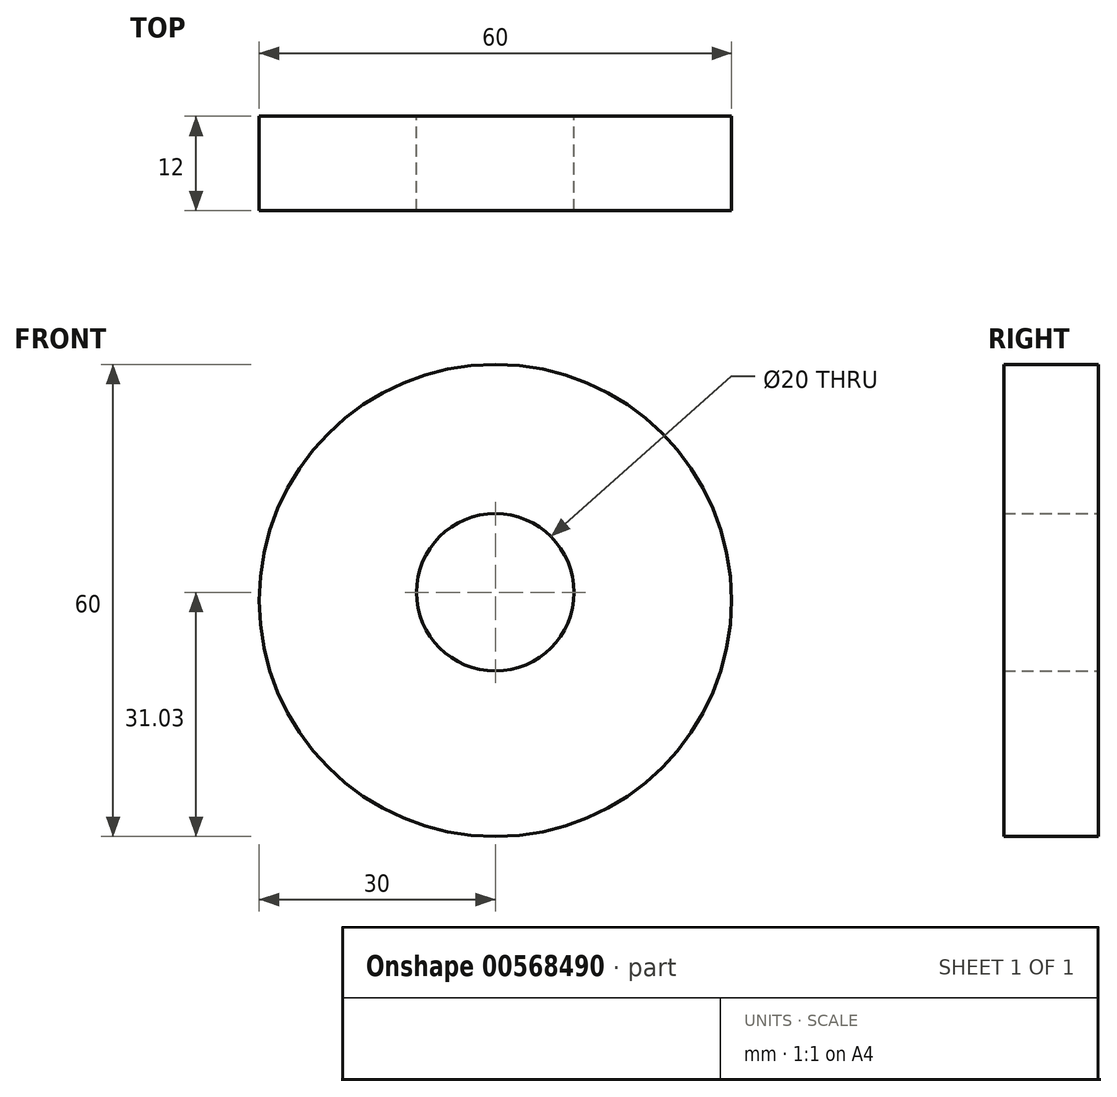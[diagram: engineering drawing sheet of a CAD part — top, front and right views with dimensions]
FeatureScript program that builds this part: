
annotation { "Feature Type Name" : "Feature", "Feature Type Description" : "" }
export const myFeature = defineFeature(function(context is Context, id is Id, definition is map)
    precondition{}
    {
        {
            var Q0;
            Q0=qCreatedBy(makeId("Front.planeOp"),FACE);
            var sketch = newSketch(context, id + "F0", { "sketchPlane" : qUnion([Q0])});
            skCircle(sketch, "E0", {"center": v(0, -1.03) * mm, "radius": 30 * mm});
            skCircle(sketch, "E1", {"center": v(0, 0) * mm, "radius": 10 * mm});
            skSolve(sketch);
        }
        {
            var Q0;
            Q0=makeQuery(id+"F0.imprint","IMPRINT",FACE,{"disambiguationData":[TD([[makeQuery(id+"F0.imprint","IMPRINT",EDGE,{"derivedFrom":sQuery(id+"F0.wireOp",EDGE,"E0")}),1.0]])]});
            extrude(context, id + "F1", {"entities" : qUnion([Q0]), "endBound" : BoundingType.SYMMETRIC, "depth" : 12 * mm, "offsetDistance" : 25 * mm});
        }
    });
